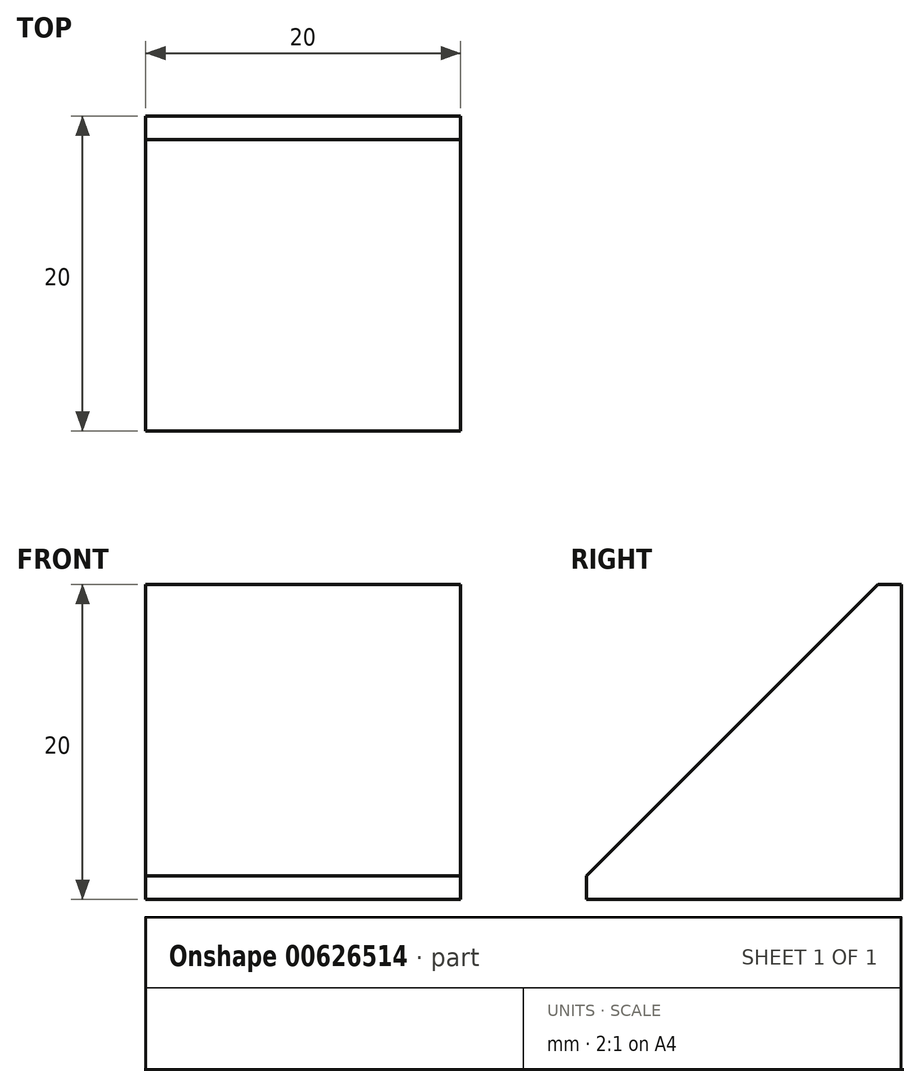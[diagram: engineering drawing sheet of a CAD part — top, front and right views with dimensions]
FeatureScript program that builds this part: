
annotation { "Feature Type Name" : "Feature", "Feature Type Description" : "" }
export const myFeature = defineFeature(function(context is Context, id is Id, definition is map)
    precondition{}
    {
        {
            var Q0;
            Q0=qCreatedBy(makeId("Right.planeOp"),FACE);
            var sketch = newSketch(context, id + "F0", { "sketchPlane" : qUnion([Q0]), "asVersion" : FeatureScriptVersionNumber.V275_SKETCH_PATTERN_LOWER_LIMIT});
            skLineSegment(sketch, "E0", {"start": v(0, 0) * mm, "end": v(0, 20) * mm});
            skLineSegment(sketch, "E1", {"start": v(0, 20) * mm, "end": v(-1.5, 20) * mm});
            skLineSegment(sketch, "E2", {"start": v(-1.5, 20) * mm, "end": v(-20, 1.5) * mm});
            skLineSegment(sketch, "E3", {"start": v(-20, 1.5) * mm, "end": v(-20, 0) * mm});
            skLineSegment(sketch, "E4", {"start": v(-20, 0) * mm, "end": v(0, 0) * mm});
            skSolve(sketch);
        }
        {
            var Q0;
            Q0=makeQuery(id+"F0.imprint","IMPRINT",FACE,{"disambiguationData":[TD([[makeQuery(id+"F0.imprint","IMPRINT",EDGE,{"derivedFrom":sQuery(id+"F0.wireOp",EDGE,"E0")}),1.0]])]});
            extrude(context, id + "F1", {"entities" : qUnion([Q0]), "depth" : 20 * mm, "symmetric" : true});
        }
    });
